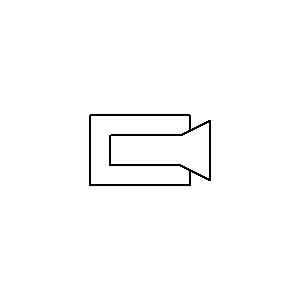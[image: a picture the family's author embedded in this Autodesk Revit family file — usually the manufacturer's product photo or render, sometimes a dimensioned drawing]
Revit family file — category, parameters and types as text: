
# Revit family: Gira_126565
name_source: partatom
category: Electrical Fixtures
revit_build: Autodesk Revit 2017 (Build: 20160225_1515(x64)
units: mm (PartAtom-declared; Revit-internal decimal feet)

## family parameters
Cut with Voids When Loaded = No
Host = Face
Maintain Annotation Orientation = Yes
Part Type = Normal
Room Calculation Point = No
Round Connector Dimension = Use Diameter
Shared = No

## types (1)
- Colour camera door st. Gira TX_44 (WP FM) c.alum.
    Available = No
    BIM (1) = https://media.stage.bim.site
    Category = External camera door communication
    Colour = Silver
    Data sheet (1) = https://katalog.gira.de
    Default Elevation = 1219 mm
    Description = Colour camera door st. TX_44 CAl,Colour camera for door station,,colour aluminium,Features:,- Installation in a conventional flush-mounted device box.,- Fits in the cover frames of the Gira TX_44 switch range.,- Modular design, allowing easy installation and expandability.,- Signal transmission and supply of the audio and video components via reverse-polarity-protected and short-circuit-proof 2-wire bus.,- Extension of door stations by a colour camera with automatic day or night switching.,- LEDs ensure steady illumination of the field of view at close proximity in night mode.,- Camera can be manually swivelled 20 horizontally and vertically. In combination with the wide-angle lens, a very wide field of view of the door entry area results.,- Automatic background lighting compensation.,- Automatic white balance.,- Automatic gain control (AGC).,- Integrated temperature-dependent camera heating.,- Sprayed-water proof cover plate.,- Camera cover plate made of shock-resistant plastic. Easy to replace if damaged, e.g. due to vandalism.,,Notes :,- The colour camera may not be positioned directly beneath a light.,- Suitable for use in a Gira energy profile.,- Not suitable for use in a Gira energy profile with light.
    GTIN = 4010337265658
    HAN = 126565
    HeinzeBIM = https://bimportal.heinze.de
    Installation technique = Bus system
    Manufacturer = Gira
    Manufacturer URL = https://www.gira.de
    Material = Other
    Mounting method = Built-in
    Name = Colour camera door st. Gira TX_44 (WP FM) c.alum.
    URL = http://katalog.gira.de

## geometry (parser evidence)
native form markers: Sweep x2
no freeform markers — native parametric forms only
